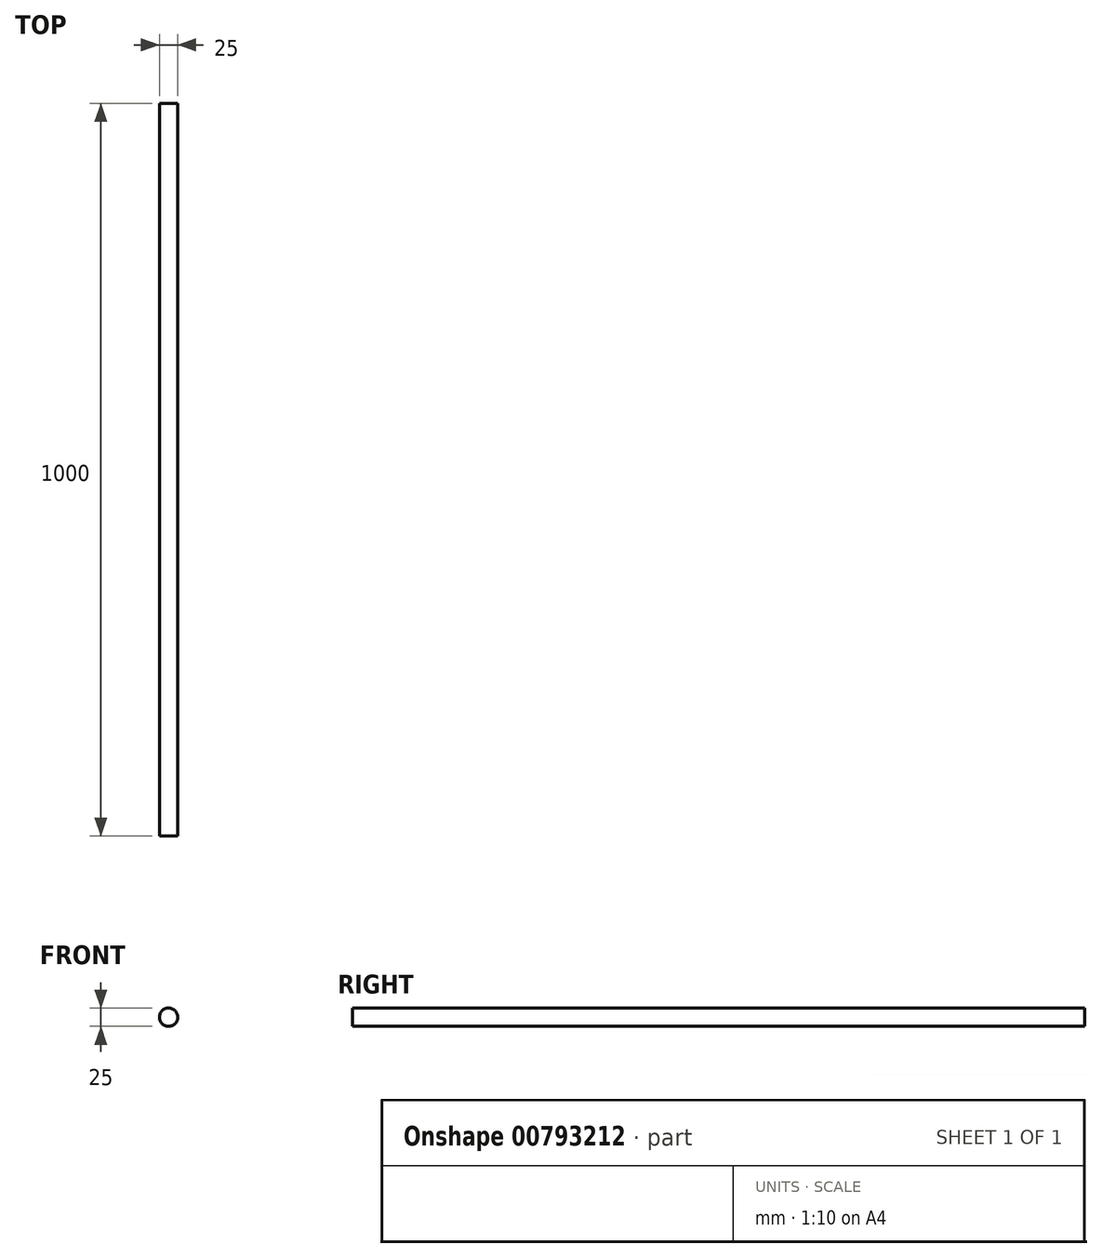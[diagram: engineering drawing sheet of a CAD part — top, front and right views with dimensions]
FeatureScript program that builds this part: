
annotation { "Feature Type Name" : "Feature", "Feature Type Description" : "" }
export const myFeature = defineFeature(function(context is Context, id is Id, definition is map)
    precondition{}
    {
        {
            var Q0;
            Q0=qCreatedBy(makeId("Front.planeOp"),FACE);
            var sketch = newSketch(context, id + "F0", { "sketchPlane" : qUnion([Q0])});
            skCircle(sketch, "E0", {"center": v(0, 0) * mm, "radius": 12.5 * mm});
            skSolve(sketch);
        }
        {
            var Q0;
            Q0=makeQuery(id+"F0.imprint","IMPRINT",FACE,{"disambiguationData":[TD([[makeQuery(id+"F0.imprint","IMPRINT",EDGE,{"derivedFrom":sQuery(id+"F0.wireOp",EDGE,"E0")}),1.0]])]});
            extrude(context, id + "F1", {"entities" : qUnion([Q0]), "depth" : 1000 * mm, "offsetDistance" : 25 * mm});
        }
    });
